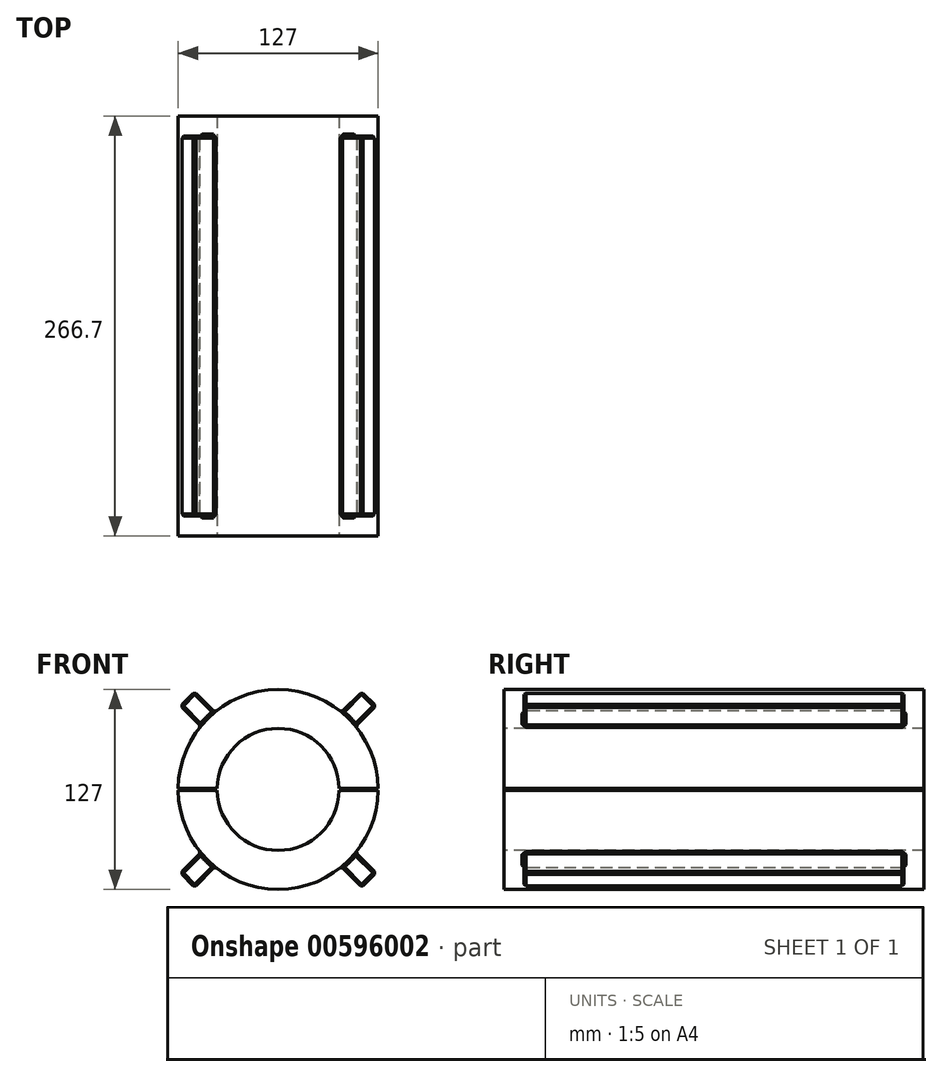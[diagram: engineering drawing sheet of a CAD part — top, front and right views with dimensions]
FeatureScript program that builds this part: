
annotation { "Feature Type Name" : "Feature", "Feature Type Description" : "" }
export const myFeature = defineFeature(function(context is Context, id is Id, definition is map)
    precondition{}
    {
        {
            var Q0;
            Q0=qCreatedBy(makeId("Front.planeOp"),FACE);
            var sketch = newSketch(context, id + "F0", { "sketchPlane" : qUnion([Q0])});
            skArc(sketch, "E0", {"start": v(-49.17, 40.19) * mm, "mid": v(-63.5, 0) * mm, "end": v(-49.17, -40.19) * mm});
            skLineSegment(sketch, "E1", {"start": v(-63.5, 0) * mm, "end": v(63.5, 0) * mm, "construction": true});
            skLineSegment(sketch, "E2", {"start": v(0, 63.5) * mm, "end": v(0, -63.5) * mm, "construction": true});
            skLineSegment(sketch, "E3", {"start": v(-75.84, -75.84) * mm, "end": v(62.04, 62.04) * mm, "construction": true});
            skLineSegment(sketch, "E4.MirrorCS", {"start": v(75.84, -75.84) * mm, "end": v(-62.04, 62.04) * mm, "construction": true});
            skLineSegment(sketch, "E5", {"start": v(53.06, 71.02) * mm, "end": v(71.02, 53.06) * mm, "construction": true});
            skCircle(sketch, "E6", {"center": v(0, 0) * mm, "radius": 69.85 * mm, "construction": true});
            skLineSegment(sketch, "E7", {"start": v(53.06, 71.02) * mm, "end": v(39.59, 57.55) * mm, "construction": true});
            skLineSegment(sketch, "E8", {"start": v(71.02, 53.06) * mm, "end": v(57.55, 39.59) * mm, "construction": true});
            skLineSegment(sketch, "E9", {"start": v(40.19, 49.17) * mm, "end": v(53.06, 62.04) * mm});
            skLineSegment(sketch, "E10", {"start": v(53.06, 62.04) * mm, "end": v(62.04, 53.06) * mm});
            skLineSegment(sketch, "E11", {"start": v(62.04, 53.06) * mm, "end": v(49.17, 40.19) * mm});
            skLineSegment(sketch, "E12.MirrorCS", {"start": v(-40.19, 49.17) * mm, "end": v(-53.06, 62.04) * mm});
            skLineSegment(sketch, "E13.MirrorCS", {"start": v(-62.04, 53.06) * mm, "end": v(-49.17, 40.19) * mm});
            skLineSegment(sketch, "E14.MirrorCS", {"start": v(-53.06, 62.04) * mm, "end": v(-62.04, 53.06) * mm});
            skLineSegment(sketch, "E15.MirrorCS", {"start": v(-62.04, -53.06) * mm, "end": v(-49.17, -40.19) * mm});
            skLineSegment(sketch, "E16.MirrorCS", {"start": v(-53.06, -62.04) * mm, "end": v(-62.04, -53.06) * mm});
            skLineSegment(sketch, "E17.MirrorCS", {"start": v(-40.19, -49.17) * mm, "end": v(-53.06, -62.04) * mm});
            skLineSegment(sketch, "E18.MirrorCS", {"start": v(40.19, -49.17) * mm, "end": v(53.06, -62.04) * mm});
            skLineSegment(sketch, "E19.MirrorCS", {"start": v(53.06, -62.04) * mm, "end": v(62.04, -53.06) * mm});
            skLineSegment(sketch, "E20.MirrorCS", {"start": v(62.04, -53.06) * mm, "end": v(49.17, -40.19) * mm});
            skArc(sketch, "E21.trimOffspring", {"start": v(40.19, 49.17) * mm, "mid": v(0, 63.5) * mm, "end": v(-40.19, 49.17) * mm});
            skArc(sketch, "E22.trimOffspring", {"start": v(-40.19, -49.17) * mm, "mid": v(0, -63.5) * mm, "end": v(40.19, -49.17) * mm});
            skArc(sketch, "E23.trimOffspring", {"start": v(49.17, -40.19) * mm, "mid": v(63.5, 0) * mm, "end": v(49.17, 40.19) * mm});
            skSolve(sketch);
        }
        {
            var Q0;
            Q0 = qSketchRegion(id + "F0", true);
            extrude(context, id + "F1", {"entities" : qUnion([Q0]), "oppositeDirection" : true, "depth" : 241.3 * mm, "offsetDistance" : 25.4 * mm});
        }
        {
            var Q0;
            Q0=makeQuery(id+"F1.opExtrude","CAP_FACE",FACE,{"disambiguationData":[OSD([sQuery(id+"F0.wireOp",EDGE,"E0"),sQuery(id+"F0.wireOp",EDGE,"E9"),sQuery(id+"F0.wireOp",EDGE,"E10"),sQuery(id+"F0.wireOp",EDGE,"E11"),sQuery(id+"F0.wireOp",EDGE,"E12.MirrorCS"),sQuery(id+"F0.wireOp",EDGE,"E13.MirrorCS"),sQuery(id+"F0.wireOp",EDGE,"E14.MirrorCS"),sQuery(id+"F0.wireOp",EDGE,"E15.MirrorCS"),sQuery(id+"F0.wireOp",EDGE,"E16.MirrorCS"),sQuery(id+"F0.wireOp",EDGE,"E17.MirrorCS"),sQuery(id+"F0.wireOp",EDGE,"E18.MirrorCS"),sQuery(id+"F0.wireOp",EDGE,"E19.MirrorCS"),sQuery(id+"F0.wireOp",EDGE,"E20.MirrorCS"),sQuery(id+"F0.wireOp",EDGE,"E21.trimOffspring"),sQuery(id+"F0.wireOp",EDGE,"E22.trimOffspring"),sQuery(id+"F0.wireOp",EDGE,"E23.trimOffspring")])],"isStart":true});
            cPlane(context, id + "F2", {"entities" : qUnion([Q0]), "cplaneType" : CPlaneType.OFFSET, "offset" : 12.7 * mm, "width" : 152.4 * mm, "height" : 152.4 * mm});
        }
        {
            var Q0;
            Q0=qCreatedBy(id+"F2.planeOp",FACE);
            var sketch = newSketch(context, id + "F3", { "sketchPlane" : qUnion([Q0])});
            skCircle(sketch, "E24", {"center": v(0, 0) * mm, "radius": 63.5 * mm});
            skSolve(sketch);
        }
        {
            var Q0;
            Q0 = qSketchRegion(id + "F3", true);
            extrude(context, id + "F4", {"entities" : qUnion([Q0]), "operationType" : NewBodyOperationType.ADD, "oppositeDirection" : true, "depth" : 266.7 * mm, "offsetDistance" : 25.4 * mm});
        }
        {
            var Q0;
            Q0=makeQuery(id+"F4.opExtrude","CAP_FACE",FACE,{"disambiguationData":[OSD([sQuery(id+"F3.wireOp",EDGE,"E24")])],"isStart":true});
            var sketch = newSketch(context, id + "F5", { "sketchPlane" : qUnion([Q0])});
            skLineSegment(sketch, "E25", {"start": v(63.5, 0) * mm, "end": v(-63.5, 0) * mm, "construction": true});
            skLineSegment(sketch, "E26", {"start": v(63.5, -0.64) * mm, "end": v(-63.5, -0.64) * mm});
            skLineSegment(sketch, "E27.MirrorCS", {"start": v(63.5, 0.64) * mm, "end": v(-63.5, 0.64) * mm});
            skLineSegment(sketch, "E28", {"start": v(63.5, -0.64) * mm, "end": v(63.5, 0.64) * mm});
            skLineSegment(sketch, "E29", {"start": v(-63.5, -0.64) * mm, "end": v(-63.5, 0.64) * mm});
            skSolve(sketch);
        }
        {
            var Q0;
            Q0 = qSketchRegion(id + "F5", true);
            extrude(context, id + "F6", {"entities" : qUnion([Q0]), "operationType" : NewBodyOperationType.REMOVE, "endBound" : BoundingType.THROUGH_ALL, "oppositeDirection" : true, "depth" : 25.4 * mm, "offsetDistance" : 25.4 * mm});
        }
        {
            var Q0;
            Q0=makeQuery(id+"F1.opExtrude","SWEPT_EDGE",EDGE,{"disambiguationData":[OSD([sQuery(id+"F0.wireOp",EDGE,"E19.MirrorCS"),sQuery(id+"F0.wireOp",EDGE,"E20.MirrorCS")])]});
            var Q1;
            Q1=makeQuery(id+"F1.opExtrude","SWEPT_EDGE",EDGE,{"disambiguationData":[OSD([sQuery(id+"F0.wireOp",EDGE,"E18.MirrorCS"),sQuery(id+"F0.wireOp",EDGE,"E19.MirrorCS")])]});
            var Q2;
            Q2=makeQuery(id+"F1.opExtrude","CAP_EDGE",EDGE,{"disambiguationData":[OSD([sQuery(id+"F0.wireOp",EDGE,"E18.MirrorCS")])],"isStart":true});
            var Q3;
            Q3=makeQuery(id+"F1.opExtrude","CAP_EDGE",EDGE,{"disambiguationData":[OSD([sQuery(id+"F0.wireOp",EDGE,"E19.MirrorCS")])],"isStart":true});
            var Q4;
            Q4=makeQuery(id+"F1.opExtrude","SWEPT_EDGE",EDGE,{"disambiguationData":[OSD([sQuery(id+"F0.wireOp",EDGE,"E20.MirrorCS"),sQuery(id+"F0.wireOp",EDGE,"E23.trimOffspring")])]});
            var Q5;
            Q5=makeQuery(id+"F1.opExtrude","CAP_EDGE",EDGE,{"disambiguationData":[OSD([sQuery(id+"F0.wireOp",EDGE,"E20.MirrorCS")])],"isStart":true});
            var Q6;
            Q6=makeQuery(id+"F4.boolean.opBoolean","INTERSECT",EDGE,{"disambiguationData":[OD(3.0)],"derivedFrom":[makeQuery(id+"F1.opExtrude","CAP_FACE",FACE,{"disambiguationData":[OSD([sQuery(id+"F0.wireOp",EDGE,"E0"),sQuery(id+"F0.wireOp",EDGE,"E9"),sQuery(id+"F0.wireOp",EDGE,"E10"),sQuery(id+"F0.wireOp",EDGE,"E11"),sQuery(id+"F0.wireOp",EDGE,"E12.MirrorCS"),sQuery(id+"F0.wireOp",EDGE,"E13.MirrorCS"),sQuery(id+"F0.wireOp",EDGE,"E14.MirrorCS"),sQuery(id+"F0.wireOp",EDGE,"E15.MirrorCS"),sQuery(id+"F0.wireOp",EDGE,"E16.MirrorCS"),sQuery(id+"F0.wireOp",EDGE,"E17.MirrorCS"),sQuery(id+"F0.wireOp",EDGE,"E18.MirrorCS"),sQuery(id+"F0.wireOp",EDGE,"E19.MirrorCS"),sQuery(id+"F0.wireOp",EDGE,"E20.MirrorCS"),sQuery(id+"F0.wireOp",EDGE,"E21.trimOffspring"),sQuery(id+"F0.wireOp",EDGE,"E22.trimOffspring"),sQuery(id+"F0.wireOp",EDGE,"E23.trimOffspring")])],"isStart":true}),makeQuery(id+"F4.opExtrude","SWEPT_FACE",FACE,{"disambiguationData":[OSD([sQuery(id+"F3.wireOp",EDGE,"E24")])]})]});
            var Q7;
            Q7=makeQuery(id+"F1.opExtrude","SWEPT_EDGE",EDGE,{"disambiguationData":[OSD([sQuery(id+"F0.wireOp",EDGE,"E18.MirrorCS"),sQuery(id+"F0.wireOp",EDGE,"E22.trimOffspring")])]});
            var Q8;
            Q8=makeQuery(id+"F1.opExtrude","CAP_EDGE",EDGE,{"disambiguationData":[OSD([sQuery(id+"F0.wireOp",EDGE,"E18.MirrorCS")])],"isStart":false});
            var Q9;
            Q9=makeQuery(id+"F4.boolean.opBoolean","INTERSECT",EDGE,{"disambiguationData":[OD(3.0)],"derivedFrom":[makeQuery(id+"F1.opExtrude","CAP_FACE",FACE,{"disambiguationData":[OSD([sQuery(id+"F0.wireOp",EDGE,"E0"),sQuery(id+"F0.wireOp",EDGE,"E9"),sQuery(id+"F0.wireOp",EDGE,"E10"),sQuery(id+"F0.wireOp",EDGE,"E11"),sQuery(id+"F0.wireOp",EDGE,"E12.MirrorCS"),sQuery(id+"F0.wireOp",EDGE,"E13.MirrorCS"),sQuery(id+"F0.wireOp",EDGE,"E14.MirrorCS"),sQuery(id+"F0.wireOp",EDGE,"E15.MirrorCS"),sQuery(id+"F0.wireOp",EDGE,"E16.MirrorCS"),sQuery(id+"F0.wireOp",EDGE,"E17.MirrorCS"),sQuery(id+"F0.wireOp",EDGE,"E18.MirrorCS"),sQuery(id+"F0.wireOp",EDGE,"E19.MirrorCS"),sQuery(id+"F0.wireOp",EDGE,"E20.MirrorCS"),sQuery(id+"F0.wireOp",EDGE,"E21.trimOffspring"),sQuery(id+"F0.wireOp",EDGE,"E22.trimOffspring"),sQuery(id+"F0.wireOp",EDGE,"E23.trimOffspring")])],"isStart":false}),makeQuery(id+"F4.opExtrude","SWEPT_FACE",FACE,{"disambiguationData":[OSD([sQuery(id+"F3.wireOp",EDGE,"E24")])]})]});
            var Q10;
            Q10=makeQuery(id+"F1.opExtrude","CAP_EDGE",EDGE,{"disambiguationData":[OSD([sQuery(id+"F0.wireOp",EDGE,"E19.MirrorCS")])],"isStart":false});
            var Q11;
            Q11=makeQuery(id+"F1.opExtrude","CAP_EDGE",EDGE,{"disambiguationData":[OSD([sQuery(id+"F0.wireOp",EDGE,"E20.MirrorCS")])],"isStart":false});
            var Q12;
            Q12=makeQuery(id+"F4.boolean.opBoolean","INTERSECT",EDGE,{"disambiguationData":[OD(1.0)],"derivedFrom":[makeQuery(id+"F1.opExtrude","CAP_FACE",FACE,{"disambiguationData":[OSD([sQuery(id+"F0.wireOp",EDGE,"E0"),sQuery(id+"F0.wireOp",EDGE,"E9"),sQuery(id+"F0.wireOp",EDGE,"E10"),sQuery(id+"F0.wireOp",EDGE,"E11"),sQuery(id+"F0.wireOp",EDGE,"E12.MirrorCS"),sQuery(id+"F0.wireOp",EDGE,"E13.MirrorCS"),sQuery(id+"F0.wireOp",EDGE,"E14.MirrorCS"),sQuery(id+"F0.wireOp",EDGE,"E15.MirrorCS"),sQuery(id+"F0.wireOp",EDGE,"E16.MirrorCS"),sQuery(id+"F0.wireOp",EDGE,"E17.MirrorCS"),sQuery(id+"F0.wireOp",EDGE,"E18.MirrorCS"),sQuery(id+"F0.wireOp",EDGE,"E19.MirrorCS"),sQuery(id+"F0.wireOp",EDGE,"E20.MirrorCS"),sQuery(id+"F0.wireOp",EDGE,"E21.trimOffspring"),sQuery(id+"F0.wireOp",EDGE,"E22.trimOffspring"),sQuery(id+"F0.wireOp",EDGE,"E23.trimOffspring")])],"isStart":false}),makeQuery(id+"F4.opExtrude","SWEPT_FACE",FACE,{"disambiguationData":[OSD([sQuery(id+"F3.wireOp",EDGE,"E24")])]})]});
            var Q13;
            Q13=makeQuery(id+"F1.opExtrude","CAP_EDGE",EDGE,{"disambiguationData":[OSD([sQuery(id+"F0.wireOp",EDGE,"E16.MirrorCS")])],"isStart":false});
            var Q14;
            Q14=makeQuery(id+"F1.opExtrude","CAP_EDGE",EDGE,{"disambiguationData":[OSD([sQuery(id+"F0.wireOp",EDGE,"E17.MirrorCS")])],"isStart":false});
            var Q15;
            Q15=makeQuery(id+"F1.opExtrude","CAP_EDGE",EDGE,{"disambiguationData":[OSD([sQuery(id+"F0.wireOp",EDGE,"E15.MirrorCS")])],"isStart":false});
            var Q16;
            Q16=makeQuery(id+"F1.opExtrude","SWEPT_EDGE",EDGE,{"disambiguationData":[OSD([sQuery(id+"F0.wireOp",EDGE,"E16.MirrorCS"),sQuery(id+"F0.wireOp",EDGE,"E17.MirrorCS")])]});
            var Q17;
            Q17=makeQuery(id+"F1.opExtrude","SWEPT_EDGE",EDGE,{"disambiguationData":[OSD([sQuery(id+"F0.wireOp",EDGE,"E15.MirrorCS"),sQuery(id+"F0.wireOp",EDGE,"E16.MirrorCS")])]});
            var Q18;
            Q18=makeQuery(id+"F1.opExtrude","SWEPT_EDGE",EDGE,{"disambiguationData":[OSD([sQuery(id+"F0.wireOp",EDGE,"E0"),sQuery(id+"F0.wireOp",EDGE,"E15.MirrorCS")])]});
            var Q19;
            Q19=makeQuery(id+"F1.opExtrude","SWEPT_EDGE",EDGE,{"disambiguationData":[OSD([sQuery(id+"F0.wireOp",EDGE,"E17.MirrorCS"),sQuery(id+"F0.wireOp",EDGE,"E22.trimOffspring")])]});
            var Q20;
            Q20=makeQuery(id+"F4.boolean.opBoolean","INTERSECT",EDGE,{"disambiguationData":[OD(1.0)],"derivedFrom":[makeQuery(id+"F1.opExtrude","CAP_FACE",FACE,{"disambiguationData":[OSD([sQuery(id+"F0.wireOp",EDGE,"E0"),sQuery(id+"F0.wireOp",EDGE,"E9"),sQuery(id+"F0.wireOp",EDGE,"E10"),sQuery(id+"F0.wireOp",EDGE,"E11"),sQuery(id+"F0.wireOp",EDGE,"E12.MirrorCS"),sQuery(id+"F0.wireOp",EDGE,"E13.MirrorCS"),sQuery(id+"F0.wireOp",EDGE,"E14.MirrorCS"),sQuery(id+"F0.wireOp",EDGE,"E15.MirrorCS"),sQuery(id+"F0.wireOp",EDGE,"E16.MirrorCS"),sQuery(id+"F0.wireOp",EDGE,"E17.MirrorCS"),sQuery(id+"F0.wireOp",EDGE,"E18.MirrorCS"),sQuery(id+"F0.wireOp",EDGE,"E19.MirrorCS"),sQuery(id+"F0.wireOp",EDGE,"E20.MirrorCS"),sQuery(id+"F0.wireOp",EDGE,"E21.trimOffspring"),sQuery(id+"F0.wireOp",EDGE,"E22.trimOffspring"),sQuery(id+"F0.wireOp",EDGE,"E23.trimOffspring")])],"isStart":true}),makeQuery(id+"F4.opExtrude","SWEPT_FACE",FACE,{"disambiguationData":[OSD([sQuery(id+"F3.wireOp",EDGE,"E24")])]})]});
            var Q21;
            Q21=makeQuery(id+"F1.opExtrude","CAP_EDGE",EDGE,{"disambiguationData":[OSD([sQuery(id+"F0.wireOp",EDGE,"E17.MirrorCS")])],"isStart":true});
            var Q22;
            Q22=makeQuery(id+"F1.opExtrude","CAP_EDGE",EDGE,{"disambiguationData":[OSD([sQuery(id+"F0.wireOp",EDGE,"E16.MirrorCS")])],"isStart":true});
            var Q23;
            Q23=makeQuery(id+"F1.opExtrude","CAP_EDGE",EDGE,{"disambiguationData":[OSD([sQuery(id+"F0.wireOp",EDGE,"E15.MirrorCS")])],"isStart":true});
            var Q24;
            Q24=makeQuery(id+"F1.opExtrude","CAP_EDGE",EDGE,{"disambiguationData":[OSD([sQuery(id+"F0.wireOp",EDGE,"E14.MirrorCS")])],"isStart":true});
            var Q25;
            Q25=makeQuery(id+"F4.boolean.opBoolean","INTERSECT",EDGE,{"disambiguationData":[OD(0.0)],"derivedFrom":[makeQuery(id+"F1.opExtrude","CAP_FACE",FACE,{"disambiguationData":[OSD([sQuery(id+"F0.wireOp",EDGE,"E0"),sQuery(id+"F0.wireOp",EDGE,"E9"),sQuery(id+"F0.wireOp",EDGE,"E10"),sQuery(id+"F0.wireOp",EDGE,"E11"),sQuery(id+"F0.wireOp",EDGE,"E12.MirrorCS"),sQuery(id+"F0.wireOp",EDGE,"E13.MirrorCS"),sQuery(id+"F0.wireOp",EDGE,"E14.MirrorCS"),sQuery(id+"F0.wireOp",EDGE,"E15.MirrorCS"),sQuery(id+"F0.wireOp",EDGE,"E16.MirrorCS"),sQuery(id+"F0.wireOp",EDGE,"E17.MirrorCS"),sQuery(id+"F0.wireOp",EDGE,"E18.MirrorCS"),sQuery(id+"F0.wireOp",EDGE,"E19.MirrorCS"),sQuery(id+"F0.wireOp",EDGE,"E20.MirrorCS"),sQuery(id+"F0.wireOp",EDGE,"E21.trimOffspring"),sQuery(id+"F0.wireOp",EDGE,"E22.trimOffspring"),sQuery(id+"F0.wireOp",EDGE,"E23.trimOffspring")])],"isStart":true}),makeQuery(id+"F4.opExtrude","SWEPT_FACE",FACE,{"disambiguationData":[OSD([sQuery(id+"F3.wireOp",EDGE,"E24")])]})]});
            var Q26;
            Q26=makeQuery(id+"F1.opExtrude","CAP_EDGE",EDGE,{"disambiguationData":[OSD([sQuery(id+"F0.wireOp",EDGE,"E13.MirrorCS")])],"isStart":true});
            var Q27;
            Q27=makeQuery(id+"F1.opExtrude","CAP_EDGE",EDGE,{"disambiguationData":[OSD([sQuery(id+"F0.wireOp",EDGE,"E12.MirrorCS")])],"isStart":true});
            var Q28;
            Q28=makeQuery(id+"F1.opExtrude","SWEPT_EDGE",EDGE,{"disambiguationData":[OSD([sQuery(id+"F0.wireOp",EDGE,"E13.MirrorCS"),sQuery(id+"F0.wireOp",EDGE,"E14.MirrorCS")])]});
            var Q29;
            Q29=makeQuery(id+"F1.opExtrude","SWEPT_EDGE",EDGE,{"disambiguationData":[OSD([sQuery(id+"F0.wireOp",EDGE,"E12.MirrorCS"),sQuery(id+"F0.wireOp",EDGE,"E14.MirrorCS")])]});
            var Q30;
            Q30=makeQuery(id+"F1.opExtrude","SWEPT_EDGE",EDGE,{"disambiguationData":[OSD([sQuery(id+"F0.wireOp",EDGE,"E12.MirrorCS"),sQuery(id+"F0.wireOp",EDGE,"E21.trimOffspring")])]});
            var Q31;
            Q31=makeQuery(id+"F1.opExtrude","SWEPT_EDGE",EDGE,{"disambiguationData":[OSD([sQuery(id+"F0.wireOp",EDGE,"E0"),sQuery(id+"F0.wireOp",EDGE,"E13.MirrorCS")])]});
            var Q32;
            Q32=makeQuery(id+"F4.boolean.opBoolean","INTERSECT",EDGE,{"disambiguationData":[OD(0.0)],"derivedFrom":[makeQuery(id+"F1.opExtrude","CAP_FACE",FACE,{"disambiguationData":[OSD([sQuery(id+"F0.wireOp",EDGE,"E0"),sQuery(id+"F0.wireOp",EDGE,"E9"),sQuery(id+"F0.wireOp",EDGE,"E10"),sQuery(id+"F0.wireOp",EDGE,"E11"),sQuery(id+"F0.wireOp",EDGE,"E12.MirrorCS"),sQuery(id+"F0.wireOp",EDGE,"E13.MirrorCS"),sQuery(id+"F0.wireOp",EDGE,"E14.MirrorCS"),sQuery(id+"F0.wireOp",EDGE,"E15.MirrorCS"),sQuery(id+"F0.wireOp",EDGE,"E16.MirrorCS"),sQuery(id+"F0.wireOp",EDGE,"E17.MirrorCS"),sQuery(id+"F0.wireOp",EDGE,"E18.MirrorCS"),sQuery(id+"F0.wireOp",EDGE,"E19.MirrorCS"),sQuery(id+"F0.wireOp",EDGE,"E20.MirrorCS"),sQuery(id+"F0.wireOp",EDGE,"E21.trimOffspring"),sQuery(id+"F0.wireOp",EDGE,"E22.trimOffspring"),sQuery(id+"F0.wireOp",EDGE,"E23.trimOffspring")])],"isStart":false}),makeQuery(id+"F4.opExtrude","SWEPT_FACE",FACE,{"disambiguationData":[OSD([sQuery(id+"F3.wireOp",EDGE,"E24")])]})]});
            var Q33;
            Q33=makeQuery(id+"F1.opExtrude","CAP_EDGE",EDGE,{"disambiguationData":[OSD([sQuery(id+"F0.wireOp",EDGE,"E13.MirrorCS")])],"isStart":false});
            var Q34;
            Q34=makeQuery(id+"F1.opExtrude","CAP_EDGE",EDGE,{"disambiguationData":[OSD([sQuery(id+"F0.wireOp",EDGE,"E14.MirrorCS")])],"isStart":false});
            var Q35;
            Q35=makeQuery(id+"F1.opExtrude","CAP_EDGE",EDGE,{"disambiguationData":[OSD([sQuery(id+"F0.wireOp",EDGE,"E12.MirrorCS")])],"isStart":false});
            var Q36;
            Q36=makeQuery(id+"F1.opExtrude","CAP_EDGE",EDGE,{"disambiguationData":[OSD([sQuery(id+"F0.wireOp",EDGE,"E9")])],"isStart":false});
            var Q37;
            Q37=makeQuery(id+"F1.opExtrude","CAP_EDGE",EDGE,{"disambiguationData":[OSD([sQuery(id+"F0.wireOp",EDGE,"E11")])],"isStart":false});
            var Q38;
            Q38=makeQuery(id+"F4.boolean.opBoolean","INTERSECT",EDGE,{"disambiguationData":[OD(2.0)],"derivedFrom":[makeQuery(id+"F1.opExtrude","CAP_FACE",FACE,{"disambiguationData":[OSD([sQuery(id+"F0.wireOp",EDGE,"E0"),sQuery(id+"F0.wireOp",EDGE,"E9"),sQuery(id+"F0.wireOp",EDGE,"E10"),sQuery(id+"F0.wireOp",EDGE,"E11"),sQuery(id+"F0.wireOp",EDGE,"E12.MirrorCS"),sQuery(id+"F0.wireOp",EDGE,"E13.MirrorCS"),sQuery(id+"F0.wireOp",EDGE,"E14.MirrorCS"),sQuery(id+"F0.wireOp",EDGE,"E15.MirrorCS"),sQuery(id+"F0.wireOp",EDGE,"E16.MirrorCS"),sQuery(id+"F0.wireOp",EDGE,"E17.MirrorCS"),sQuery(id+"F0.wireOp",EDGE,"E18.MirrorCS"),sQuery(id+"F0.wireOp",EDGE,"E19.MirrorCS"),sQuery(id+"F0.wireOp",EDGE,"E20.MirrorCS"),sQuery(id+"F0.wireOp",EDGE,"E21.trimOffspring"),sQuery(id+"F0.wireOp",EDGE,"E22.trimOffspring"),sQuery(id+"F0.wireOp",EDGE,"E23.trimOffspring")])],"isStart":false}),makeQuery(id+"F4.opExtrude","SWEPT_FACE",FACE,{"disambiguationData":[OSD([sQuery(id+"F3.wireOp",EDGE,"E24")])]})]});
            var Q39;
            Q39=makeQuery(id+"F1.opExtrude","CAP_EDGE",EDGE,{"disambiguationData":[OSD([sQuery(id+"F0.wireOp",EDGE,"E10")])],"isStart":false});
            var Q40;
            Q40=makeQuery(id+"F1.opExtrude","SWEPT_EDGE",EDGE,{"disambiguationData":[OSD([sQuery(id+"F0.wireOp",EDGE,"E10"),sQuery(id+"F0.wireOp",EDGE,"E11")])]});
            var Q41;
            Q41=makeQuery(id+"F1.opExtrude","SWEPT_EDGE",EDGE,{"disambiguationData":[OSD([sQuery(id+"F0.wireOp",EDGE,"E9"),sQuery(id+"F0.wireOp",EDGE,"E10")])]});
            var Q42;
            Q42=makeQuery(id+"F1.opExtrude","SWEPT_EDGE",EDGE,{"disambiguationData":[OSD([sQuery(id+"F0.wireOp",EDGE,"E11"),sQuery(id+"F0.wireOp",EDGE,"E23.trimOffspring")])]});
            var Q43;
            Q43=makeQuery(id+"F1.opExtrude","SWEPT_EDGE",EDGE,{"disambiguationData":[OSD([sQuery(id+"F0.wireOp",EDGE,"E9"),sQuery(id+"F0.wireOp",EDGE,"E21.trimOffspring")])]});
            var Q44;
            Q44=makeQuery(id+"F4.boolean.opBoolean","INTERSECT",EDGE,{"disambiguationData":[OD(2.0)],"derivedFrom":[makeQuery(id+"F1.opExtrude","CAP_FACE",FACE,{"disambiguationData":[OSD([sQuery(id+"F0.wireOp",EDGE,"E0"),sQuery(id+"F0.wireOp",EDGE,"E9"),sQuery(id+"F0.wireOp",EDGE,"E10"),sQuery(id+"F0.wireOp",EDGE,"E11"),sQuery(id+"F0.wireOp",EDGE,"E12.MirrorCS"),sQuery(id+"F0.wireOp",EDGE,"E13.MirrorCS"),sQuery(id+"F0.wireOp",EDGE,"E14.MirrorCS"),sQuery(id+"F0.wireOp",EDGE,"E15.MirrorCS"),sQuery(id+"F0.wireOp",EDGE,"E16.MirrorCS"),sQuery(id+"F0.wireOp",EDGE,"E17.MirrorCS"),sQuery(id+"F0.wireOp",EDGE,"E18.MirrorCS"),sQuery(id+"F0.wireOp",EDGE,"E19.MirrorCS"),sQuery(id+"F0.wireOp",EDGE,"E20.MirrorCS"),sQuery(id+"F0.wireOp",EDGE,"E21.trimOffspring"),sQuery(id+"F0.wireOp",EDGE,"E22.trimOffspring"),sQuery(id+"F0.wireOp",EDGE,"E23.trimOffspring")])],"isStart":true}),makeQuery(id+"F4.opExtrude","SWEPT_FACE",FACE,{"disambiguationData":[OSD([sQuery(id+"F3.wireOp",EDGE,"E24")])]})]});
            var Q45;
            Q45=makeQuery(id+"F1.opExtrude","CAP_EDGE",EDGE,{"disambiguationData":[OSD([sQuery(id+"F0.wireOp",EDGE,"E9")])],"isStart":true});
            var Q46;
            Q46=makeQuery(id+"F1.opExtrude","CAP_EDGE",EDGE,{"disambiguationData":[OSD([sQuery(id+"F0.wireOp",EDGE,"E10")])],"isStart":true});
            var Q47;
            Q47=makeQuery(id+"F1.opExtrude","CAP_EDGE",EDGE,{"disambiguationData":[OSD([sQuery(id+"F0.wireOp",EDGE,"E11")])],"isStart":true});
            chamfer(context, id + "F7", {"entities" : qUnion([Q0, Q1, Q2, Q3, Q4, Q5, Q6, Q7, Q8, Q9, Q10, Q11, Q12, Q13, Q14, Q15, Q16, Q17, Q18, Q19, Q20, Q21, Q22, Q23, Q24, Q25, Q26, Q27, Q28, Q29, Q30, Q31, Q32, Q33, Q34, Q35, Q36, Q37, Q38, Q39, Q40, Q41, Q42, Q43, Q44, Q45, Q46, Q47]), "width" : 1.27 * mm, "tangentPropagation" : true});
        }
        {
            var Q0;
            Q0=qCreatedBy(id+"F2.planeOp",FACE);
            var sketch = newSketch(context, id + "F8", { "sketchPlane" : qUnion([Q0])});
            skCircle(sketch, "E30", {"center": v(0, 0) * mm, "radius": 38.73 * mm});
            skSolve(sketch);
        }
        {
            var Q0;
            Q0 = qSketchRegion(id + "F8", true);
            extrude(context, id + "F9", {"entities" : qUnion([Q0]), "operationType" : NewBodyOperationType.REMOVE, "endBound" : BoundingType.THROUGH_ALL, "oppositeDirection" : true, "depth" : 25.4 * mm, "offsetDistance" : 25.4 * mm});
        }
    });
